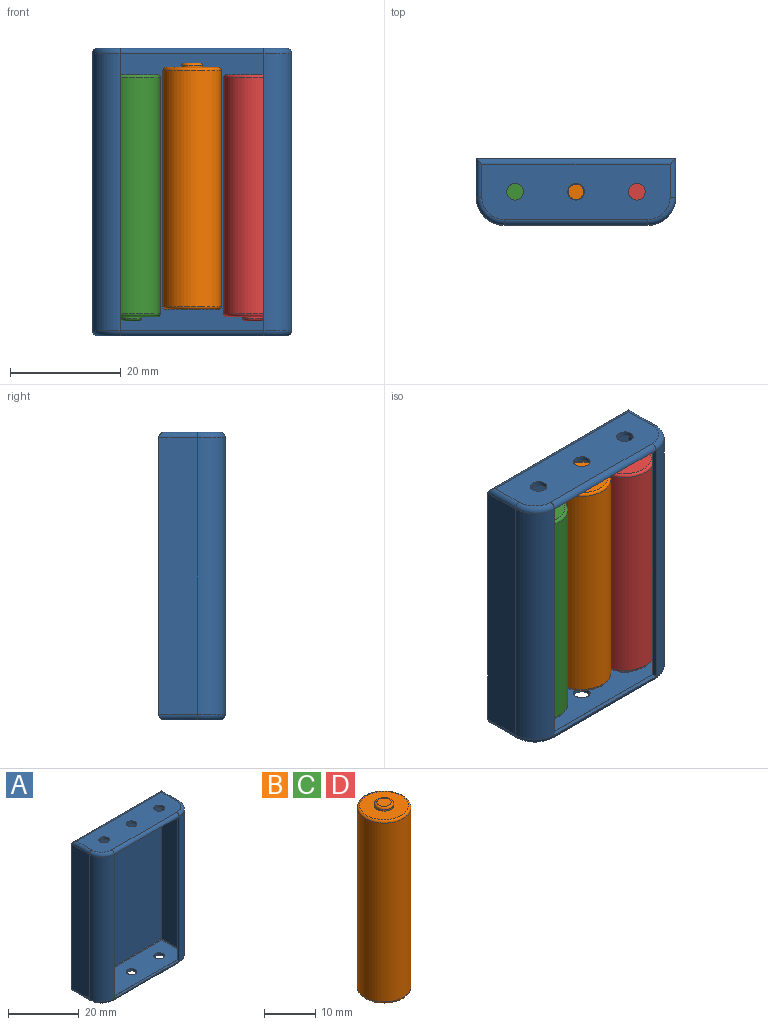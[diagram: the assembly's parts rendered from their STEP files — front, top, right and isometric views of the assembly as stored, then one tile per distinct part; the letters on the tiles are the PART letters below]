
ASSEMBLY  parts=4 mates=3
PART A: 48 faces, bbox 36.8x12.4x52 mm
  f0: plane 34x10mm, normal (0,0,1), area 311.9mm2, adj f7,f8,f9,f10,f11,f12,f45,f46
  f1: plane 50x7mm, normal (-1,0,0), area 350mm2, adj f4,f5,f10,f17
  f2: plane 34x10mm, normal (0,0,-1), area 311.9mm2, adj f13,f14,f15,f16,f17,f18,f42,f43
  f3: plane 50x7mm, normal (1,0,0), area 350mm2, adj f4,f6,f7,f13
  f4: plane 50x36mm, normal (0,1,0), area 1800mm2, adj f1,f3,f8,f15
  f5: cylinder r=5mm len=50mm, axis (0,0,1), area 392.7mm2, adj f1,f12,f18,f22
  f6: cylinder r=5mm len=50mm, axis (0,0,-1), area 392.7mm2, adj f3,f9,f14,f20
  f7: cylinder r=1mm len=7mm, axis (0,1,0), area 10.4mm2, adj f0,f3,f8,f9
  f8: cylinder r=1mm len=36mm, axis (-1,0,0), area 55.4mm2, adj f0,f4,f7,f10
  f9: torus R=4mm, axis (0,0,1), area 11.4mm2, adj f0,f6,f7,f11
  f10: cylinder r=1mm len=7mm, axis (0,-1,0), area 10.4mm2, adj f0,f1,f8,f12
  f11: cylinder r=1mm len=26mm, axis (1,0,0), area 40.8mm2, adj f0,f9,f12,f19
  f12: torus R=4mm, axis (0,0,1), area 11.4mm2, adj f0,f5,f10,f11
  f13: cylinder r=1mm len=7mm, axis (0,-1,0), area 10.4mm2, adj f2,f3,f14,f15
  f14: torus R=4mm, axis (0,0,1), area 11.4mm2, adj f2,f6,f13,f16
  f15: cylinder r=1mm len=36mm, axis (1,0,0), area 55.4mm2, adj f2,f4,f13,f17
  f16: cylinder r=1mm len=26mm, axis (-1,0,0), area 40.8mm2, adj f2,f14,f18,f21
  f17: cylinder r=1mm len=7mm, axis (0,1,0), area 10.4mm2, adj f1,f2,f15,f18
  f18: torus R=4mm, axis (0,0,1), area 11.4mm2, adj f2,f5,f16,f17
  f19: plane 26x0.8mm, normal (0,0,-1), area 20.8mm2, adj f11,f20,f22,f34
  f20: plane 50x0.8mm, normal (-1,0,0), area 40mm2, adj f6,f19,f21,f29
  f21: plane 26x0.8mm, normal (0,0,1), area 20.8mm2, adj f16,f20,f22,f39
  f22: plane 50x0.8mm, normal (1,0,0), area 40mm2, adj f5,f19,f21,f28
  f23: plane 34x10mm, normal (0,0,-1), area 311.9mm2, adj f30,f31,f32,f33,f34,f35,f45,f46
  f24: plane 50x6.2mm, normal (1,0,0), area 310mm2, adj f27,f28,f33,f40
  f25: plane 34x10mm, normal (0,0,1), area 311.9mm2, adj f36,f37,f38,f39,f40,f41,f42,f43
  f26: plane 50x6.2mm, normal (-1,0,0), area 310mm2, adj f27,f29,f30,f36
  f27: plane 50x34.4mm, normal (0,-1,0), area 1720mm2, adj f24,f26,f31,f38
  f28: cylinder r=4.2mm len=50mm, axis (0,0,1), area 329.9mm2, adj f22,f24,f35,f41
  f29: cylinder r=4.2mm len=50mm, axis (0,0,-1), area 329.9mm2, adj f20,f26,f32,f37
  f30: cylinder r=0.2mm len=6.2mm, axis (0,1,0), area 1.9mm2, adj f23,f26,f31,f32
  f31: cylinder r=0.2mm len=34.4mm, axis (-1,0,0), area 10.8mm2, adj f23,f27,f30,f33
  f32: torus R=4mm, axis (0,0,1), area 2mm2, adj f23,f29,f30,f34
  f33: cylinder r=0.2mm len=6.2mm, axis (0,-1,0), area 1.9mm2, adj f23,f24,f31,f35
  f34: cylinder r=0.2mm len=26mm, axis (1,0,0), area 8.2mm2, adj f19,f23,f32,f35
  f35: torus R=4mm, axis (0,0,1), area 2mm2, adj f23,f28,f33,f34
  f36: cylinder r=0.2mm len=6.2mm, axis (0,-1,0), area 1.9mm2, adj f25,f26,f37,f38
  f37: torus R=4mm, axis (0,0,1), area 2mm2, adj f25,f29,f36,f39
  f38: cylinder r=0.2mm len=34.4mm, axis (1,0,0), area 10.8mm2, adj f25,f27,f36,f40
  f39: cylinder r=0.2mm len=26mm, axis (-1,0,0), area 8.2mm2, adj f21,f25,f37,f41
  f40: cylinder r=0.2mm len=6.2mm, axis (0,1,0), area 1.9mm2, adj f24,f25,f38,f41
  f41: torus R=4mm, axis (0,0,1), area 2mm2, adj f25,f28,f39,f40
  f42: cylinder r=1.5mm len=3mm, axis (0,0,1), area 7.5mm2, adj f2,f25
  f43: cylinder r=1.5mm len=3mm, axis (0,0,1), area 7.5mm2, adj f2,f25
  f44: cylinder r=1.5mm len=3mm, axis (0,0,1), area 7.5mm2, adj f2,f25
  f45: cylinder r=1.5mm len=3mm, axis (0,0,1), area 7.5mm2, adj f0,f23
  f46: cylinder r=1.5mm len=3mm, axis (0,0,1), area 7.5mm2, adj f0,f23
  f47: cylinder r=1.5mm len=3mm, axis (0,0,1), area 7.5mm2, adj f0,f23
PART B: 8 faces, bbox 11.4x11.4x44.5 mm
  f0: cylinder r=5.25mm len=42.7mm, axis (0,0,-1), area 1408.5mm2, adj f6,f7
  f1: plane 9.5x9.5mm, normal (0,0,-1), area 70.9mm2, adj f7
  f2: cylinder r=1.9mm len=3.8mm, axis (0,0,1), area 3.6mm2, adj f3,f5
  f3: plane 9.5x9.5mm, normal (0,0,1), area 59.5mm2, adj f2,f6
  f4: plane 2.8x2.8mm, normal (0,0,1), area 6.2mm2, adj f5
  f5: torus R=1.4mm, axis (0,0,1), area 8.5mm2, adj f2,f4
  f6: torus R=4.75mm, axis (0,0,1), area 25mm2, adj f0,f3
  f7: torus R=4.75mm, axis (0,0,1), area 25mm2, adj f0,f1
PART C: same geometry as B
PART D: same geometry as B
PLACE A t=(0,0.8,0)mm
PLACE B t=(0,-5.2,-21.2)mm
PLACE C rot(axis=(1,0,0),180deg) t=(-11,-5.2,21.2)mm
PLACE D rot(axis=(1,0,0),180deg) t=(11,-5.2,21.2)mm
MATE fastened C.f0 <-> A.f44  axis (0,0,1) through (-11,-5.2,21.2)mm
MATE fastened B.f0 <-> A.f43  axis (0,0,-1) through (0,-5.2,-21.2)mm
MATE fastened D.f0 <-> A.f42  axis (0,0,1) through (11,-5.2,21.2)mm
